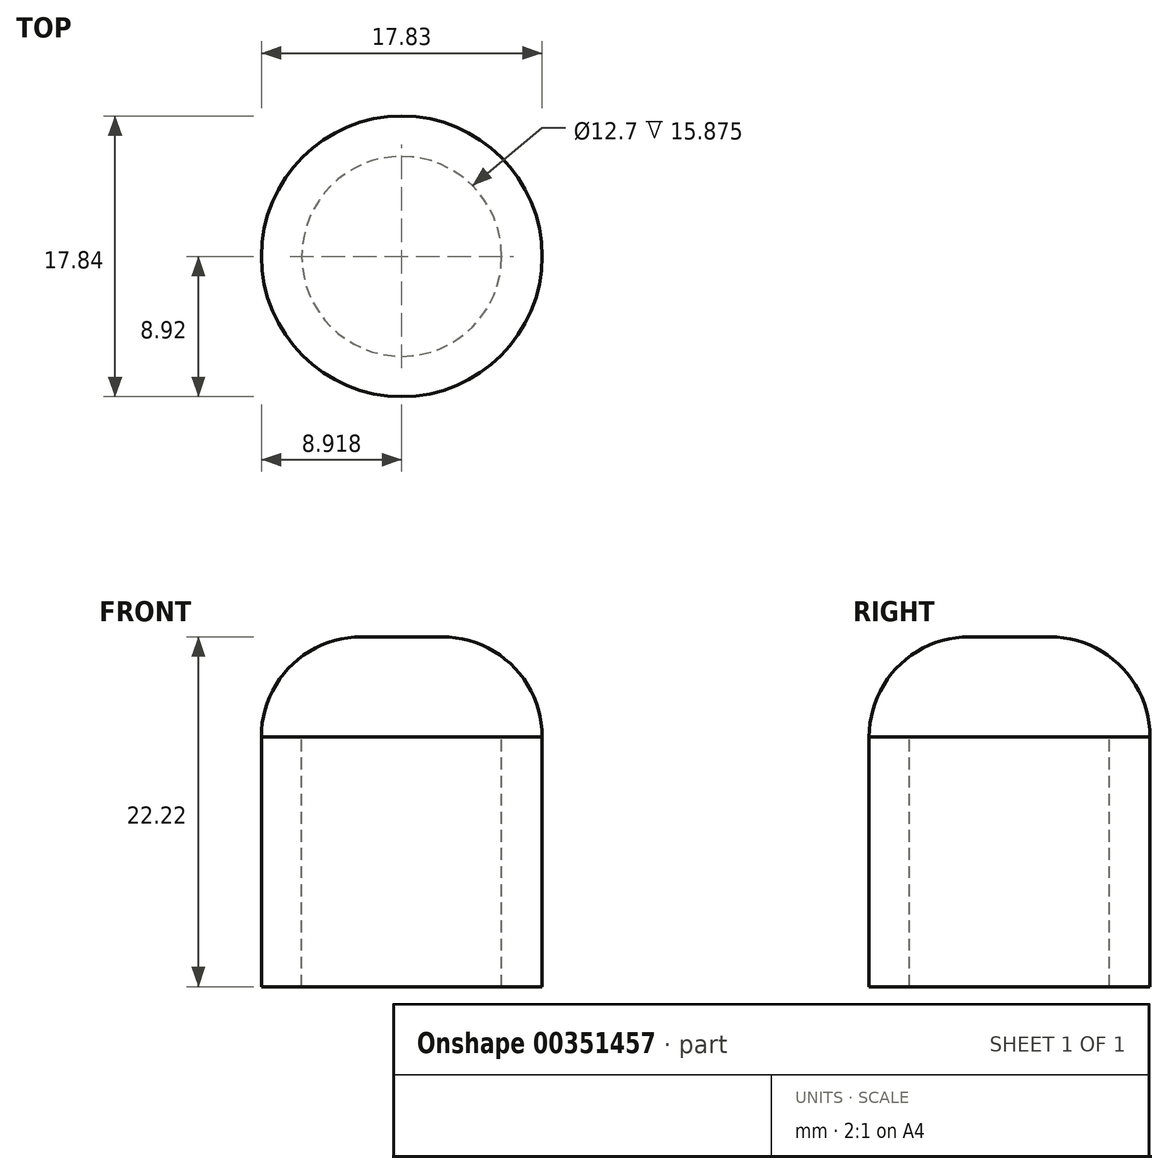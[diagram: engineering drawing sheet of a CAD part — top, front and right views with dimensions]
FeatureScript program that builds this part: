
annotation { "Feature Type Name" : "Feature", "Feature Type Description" : "" }
export const myFeature = defineFeature(function(context is Context, id is Id, definition is map)
    precondition{}
    {
        {
            var Q0;
            Q0=qCreatedBy(makeId("Front.planeOp"),FACE);
            var sketch = newSketch(context, id + "F0", { "sketchPlane" : qUnion([Q0])});
            skLineSegment(sketch, "E0.bottom", {"start": v(-28.83, 1.1) * mm, "end": v(-26.26, 1.1) * mm});
            skLineSegment(sketch, "E0.top", {"start": v(-28.83, -11.6) * mm, "end": v(-26.26, -11.6) * mm});
            skLineSegment(sketch, "E0.left", {"start": v(-28.83, 1.1) * mm, "end": v(-28.83, -11.6) * mm});
            skLineSegment(sketch, "E0.right", {"start": v(-26.26, 1.1) * mm, "end": v(-26.26, -11.6) * mm});
            skLineSegment(sketch, "E1.0", {"start": v(-19.91, 1.1) * mm, "end": v(-19.91, -11.6) * mm});
            skSolve(sketch);
        }
        {
            var Q0;
            Q0=makeQuery(id+"F0.imprint","IMPRINT",FACE,{"disambiguationData":[TD([[makeQuery(id+"F0.imprint","IMPRINT",EDGE,{"derivedFrom":sQuery(id+"F0.wireOp",EDGE,"E0.bottom")}),-1.0]])]});
            var Q1;
            Q1=sQuery(id+"F0.wireOp",EDGE,"E1.0");
            revolve(context, id + "F1", {"entities" : qUnion([Q0]), "axis" : qUnion([Q1]), "revolveType" : RevolveType.FULL});
        }
        {
            var Q0;
            Q0=makeQuery(id+"F1.opRevolve","SWEPT_FACE",FACE,{"disambiguationData":[OSD([sQuery(id+"F0.wireOp",EDGE,"E0.bottom")])]});
            var sketch = newSketch(context, id + "F2", { "sketchPlane" : qUnion([Q0])});
            skCircle(sketch, "E2.0", {"center": v(-19.91, 0) * mm, "radius": 8.92 * mm});
            skSolve(sketch);
        }
        {
            var Q0;
            Q0 = qSketchRegion(id + "F2", true);
            var Q1;
            Q1=makeQuery(id+"F2.imprint","IMPRINT",FACE,{"disambiguationData":[TD([[makeQuery(id+"F2.imprint","IMPRINT",EDGE,{"derivedFrom":makeQuery(id+"F1.opRevolve","SWEPT_EDGE",EDGE,{"disambiguationData":[OSD([sQuery(id+"F0.wireOp",EDGE,"E0.bottom"),sQuery(id+"F0.wireOp",EDGE,"E0.right")])]})}),1.0]])]});
            var Q2;
            Q2=makeQuery(id+"F2.imprint","IMPRINT",FACE,{"disambiguationData":[TD([[makeQuery(id+"F2.imprint","IMPRINT",EDGE,{"derivedFrom":sQuery(id+"F2.wireOp",EDGE,"E2.0")}),1.0]])]});
            extrude(context, id + "F3", {"entities" : qUnion([Q0, Q1, Q2]), "depth" : 6.35 * mm});
        }
        {
            var Q0;
            Q0=makeQuery(id+"F3.opExtrude","CAP_EDGE",EDGE,{"disambiguationData":[OSD([sQuery(id+"F2.wireOp",EDGE,"E2.0")])],"isStart":false});
            fillet(context, id + "F4", {"entities" : qUnion([Q0]), "radius" : 6.35 * mm, "tangentPropagation" : true, "allowEdgeOverflow" : false});
        }
        {
            var Q0;
            Q0=makeQuery(id+"F1.opRevolve","SWEPT_FACE",FACE,{"disambiguationData":[OSD([sQuery(id+"F0.wireOp",EDGE,"E0.top")])]});
            var sketch = newSketch(context, id + "F5", { "sketchPlane" : qUnion([Q0])});
            skCircle(sketch, "E3.0", {"center": v(-19.91, 0) * mm, "radius": 8.92 * mm});
            skCircle(sketch, "E4.0", {"center": v(-19.91, 0) * mm, "radius": 6.35 * mm});
            skSolve(sketch);
        }
        {
            var Q0;
            Q0 = qSketchRegion(id + "F5", true);
            var Q1;
            Q1=makeQuery(id+"F5.imprint","IMPRINT",FACE,{"disambiguationData":[TD([[makeQuery(id+"F5.imprint","IMPRINT",EDGE,{"derivedFrom":sQuery(id+"F5.wireOp",EDGE,"E3.0")}),-1.0]])]});
            extrude(context, id + "F6", {"entities" : qUnion([Q0, Q1]), "operationType" : NewBodyOperationType.ADD, "depth" : 3.17 * mm});
        }
    });
